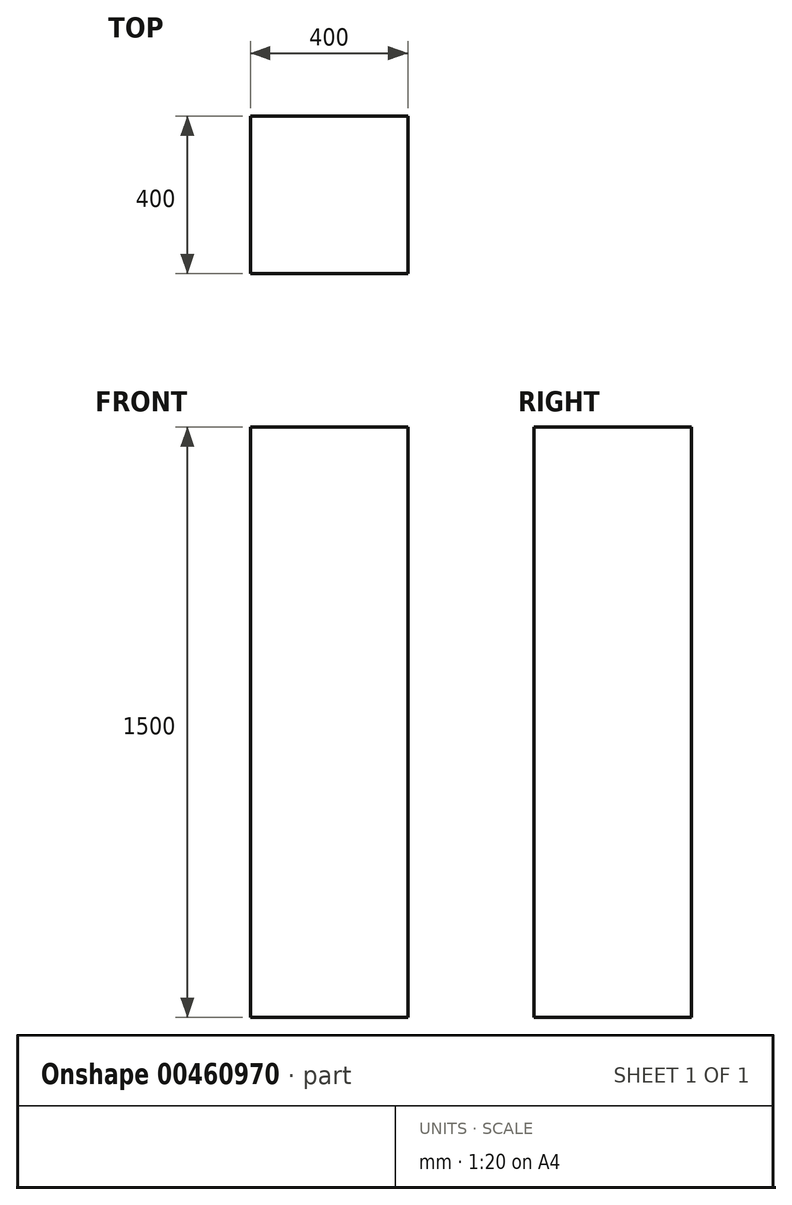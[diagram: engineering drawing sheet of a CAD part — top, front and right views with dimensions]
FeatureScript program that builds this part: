
annotation { "Feature Type Name" : "Feature", "Feature Type Description" : "" }
export const myFeature = defineFeature(function(context is Context, id is Id, definition is map)
    precondition{}
    {
        {
            var Q0;
            Q0=qCreatedBy(makeId("Top.planeOp"),FACE);
            var sketch = newSketch(context, id + "F0", { "sketchPlane" : qUnion([Q0])});
            skLineSegment(sketch, "E0.bottom", {"start": v(0, 0) * mm, "end": v(400, 0) * mm});
            skLineSegment(sketch, "E0.top", {"start": v(0, -400) * mm, "end": v(400, -400) * mm});
            skLineSegment(sketch, "E0.left", {"start": v(0, 0) * mm, "end": v(0, -400) * mm});
            skLineSegment(sketch, "E0.right", {"start": v(400, 0) * mm, "end": v(400, -400) * mm});
            skSolve(sketch);
        }
        {
            var Q0;
            Q0 = qSketchRegion(id + "F0", true);
            extrude(context, id + "F1", {"entities" : qUnion([Q0]), "depth" : 1500 * mm});
        }
    });
